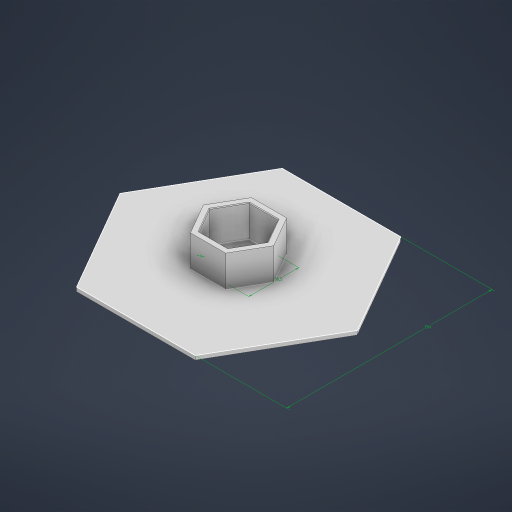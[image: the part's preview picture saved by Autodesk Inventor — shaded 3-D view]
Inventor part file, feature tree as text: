
AUTODESK INVENTOR PART (.ipt)
format: ipt  version: 2023 (Build 270158000, 158)  size: 214,016 bytes
history: native  units: mm
features: extrude x3, sketch x2, chamfer x2
ambient origin geometry x8: Origin, YZ Plane, XZ Plane, XY Plane, X Axis, Y Axis, Z Axis, Center Point
bodies: Solid1 (feature_tree)
feature tree (7):
  sketch  "Sketch1"  dims[d0=36.5mm d1=4.0mm]
  extrude  "Extrusion1"  Depth=4.0mm
  extrude  "Extrusion2"  Depth=23.0mm TaperAngle=0.0deg
  extrude  "Extrusion3"  Depth=3.0mm TaperAngle=0.0deg
  chamfer  "Chamfer1"  Distance=19.7mm
  chamfer  "Chamfer2"  Distance=18.0mm
  sketch  "Sketch2"  dims[d2=150.0mm d3=23.0mm d4=0.0mm d5=3.0mm d6=0.0mm d7=19.7mm d8=18.0mm d9=30.0mm d10=0.0mm d11=0.5mm d12=2.0mm d13=45.0deg d14=0.3mm d15=2.0mm d16=45.0deg]
